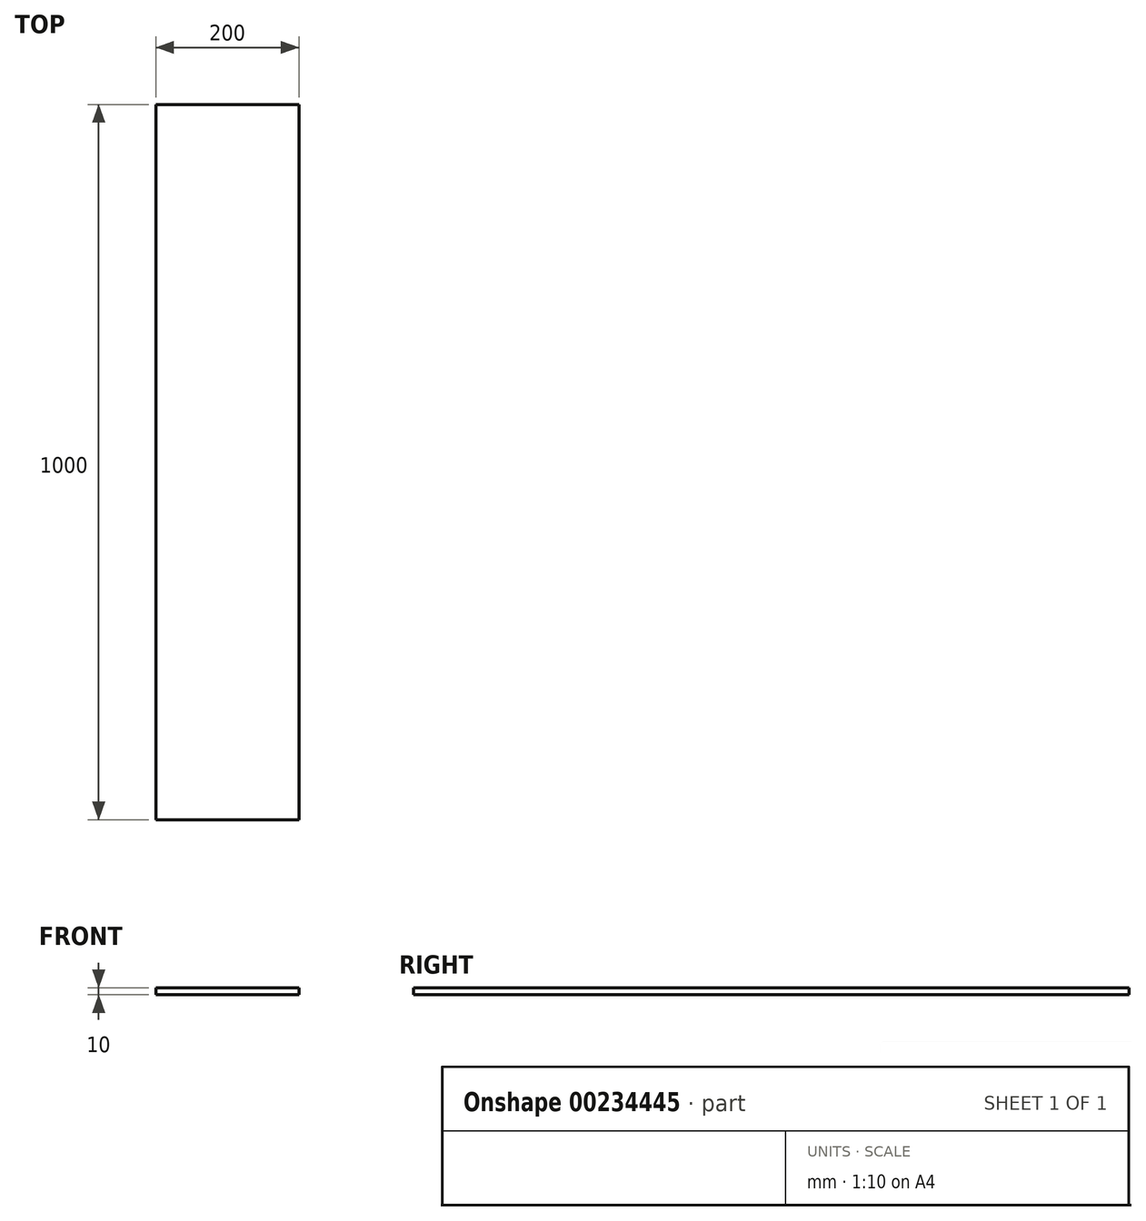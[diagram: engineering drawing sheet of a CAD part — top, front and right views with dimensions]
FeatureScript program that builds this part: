
annotation { "Feature Type Name" : "Feature", "Feature Type Description" : "" }
export const myFeature = defineFeature(function(context is Context, id is Id, definition is map)
    precondition{}
    {
        {
            var Q0;
            Q0=qCreatedBy(makeId("Top.planeOp"),FACE);
            var sketch = newSketch(context, id + "F0", { "sketchPlane" : qUnion([Q0])});
            skLineSegment(sketch, "E0.bottom", {"start": v(100, 500) * mm, "end": v(-100, 500) * mm});
            skLineSegment(sketch, "E0.top", {"start": v(100, -500) * mm, "end": v(-100, -500) * mm});
            skLineSegment(sketch, "E0.left", {"start": v(100, 500) * mm, "end": v(100, -500) * mm});
            skLineSegment(sketch, "E0.right", {"start": v(-100, 500) * mm, "end": v(-100, -500) * mm});
            skPoint(sketch, "E0.middle", {"position": v(0, 0) * mm});
            skSolve(sketch);
        }
        {
            var Q0;
            Q0 = qSketchRegion(id + "F0", true);
            extrude(context, id + "F1", {"entities" : qUnion([Q0]), "depth" : 10 * mm});
        }
    });
